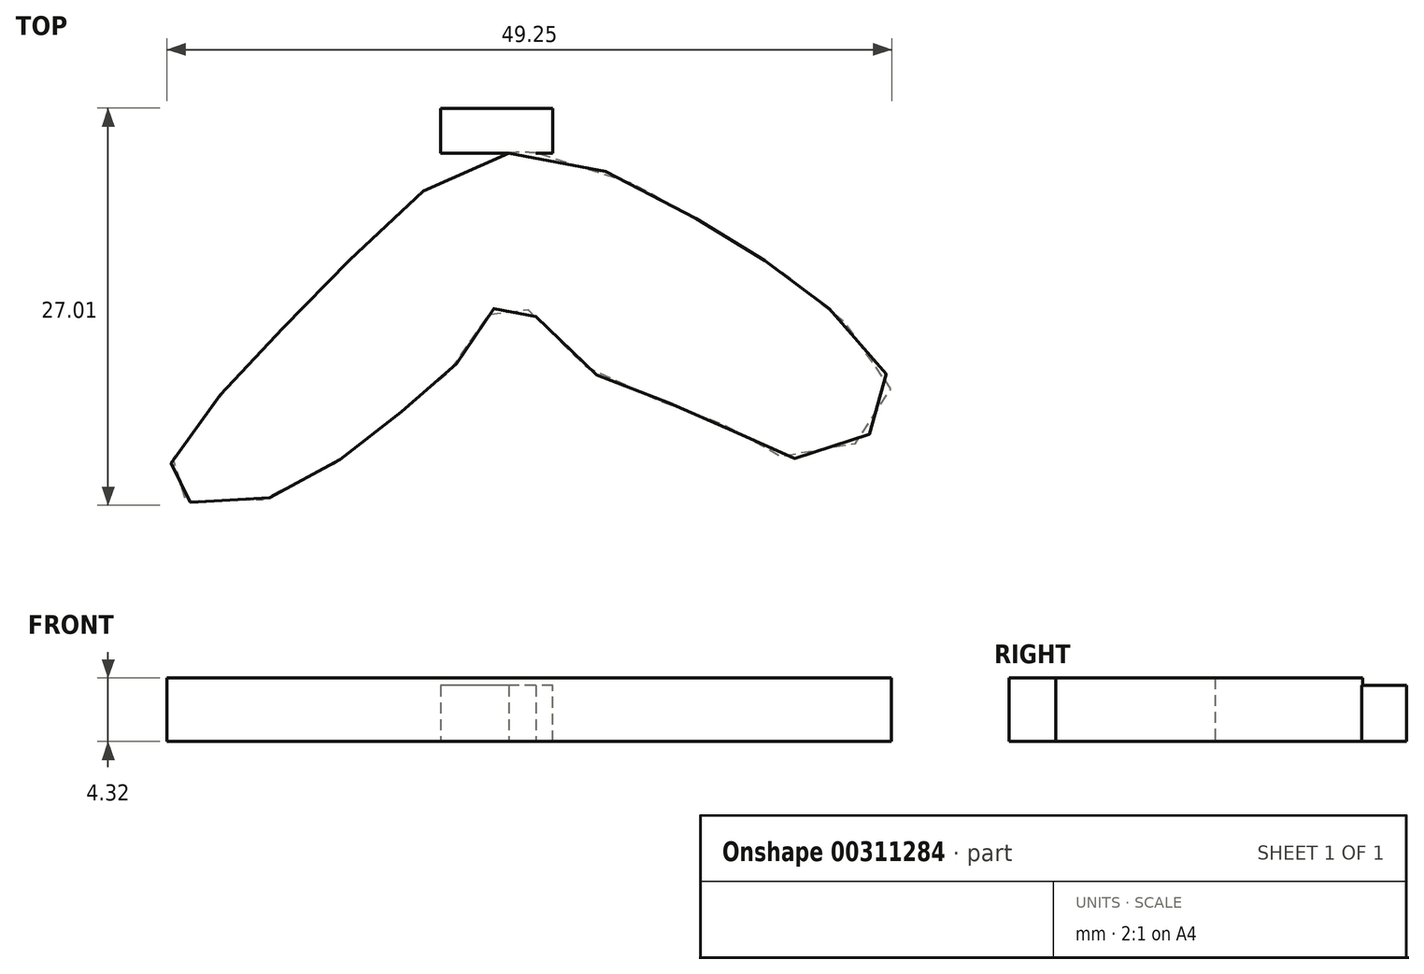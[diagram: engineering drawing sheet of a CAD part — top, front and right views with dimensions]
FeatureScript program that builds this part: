
annotation { "Feature Type Name" : "Feature", "Feature Type Description" : "" }
export const myFeature = defineFeature(function(context is Context, id is Id, definition is map)
    precondition{}
    {
        {
            var Q0;
            Q0=qCreatedBy(makeId("Top.planeOp"),FACE);
            var sketch = newSketch(context, id + "F0", { "sketchPlane" : qUnion([Q0])});
            skFitSpline(sketch, "E0", {"points": [v(0, 0) * mm, v(-11.01, -7.48) * mm, v(-19.74, -16.63) * mm, v(-23.07, -22.86) * mm, v(-16.42, -23.48) * mm, v(-8.73, -18.7) * mm, v(-2.9, -13.5) * mm, v(0, -9.98) * mm, v(5.82, -14.96) * mm, v(13.5, -17.87) * mm, v(19.53, -20.78) * mm, v(25.98, -17.04) * mm, v(20.78, -9.77) * mm, v(13.3, -4.78) * mm, v(0, 0) * mm]});
            skSolve(sketch);
        }
        {
            var Q0;
            Q0=makeQuery(id+"F0.imprint","IMPRINT",FACE,{"disambiguationData":[TD([[makeQuery(id+"F0.imprint","IMPRINT",EDGE,{"derivedFrom":sQuery(id+"F0.wireOp",EDGE,"E0")}),1.0]])]});
            extrude(context, id + "F1", {"entities" : qUnion([Q0]), "depth" : 4.32 * mm});
        }
        {
            var Q0;
            Q0=qCreatedBy(makeId("Front.planeOp"),FACE);
            var sketch = newSketch(context, id + "F2", { "sketchPlane" : qUnion([Q0])});
            skLineSegment(sketch, "E1", {"start": v(3, 0) * mm, "end": v(3, 3.81) * mm});
            skLineSegment(sketch, "E2", {"start": v(3, 3.81) * mm, "end": v(-4.61, 3.8) * mm});
            skLineSegment(sketch, "E3", {"start": v(-4.61, 3.8) * mm, "end": v(-4.61, 0) * mm});
            skLineSegment(sketch, "E4", {"start": v(-4.61, 0) * mm, "end": v(3, 0) * mm});
            skSolve(sketch);
        }
        {
            var Q0;
            Q0=makeQuery(id+"F2.imprint","IMPRINT",FACE,{"disambiguationData":[TD([[makeQuery(id+"F2.imprint","IMPRINT",EDGE,{"derivedFrom":sQuery(id+"F2.wireOp",EDGE,"E1")}),1.0]])]});
            extrude(context, id + "F3", {"entities" : qUnion([Q0]), "operationType" : NewBodyOperationType.ADD, "oppositeDirection" : true, "depth" : 3.05 * mm});
        }
    });
